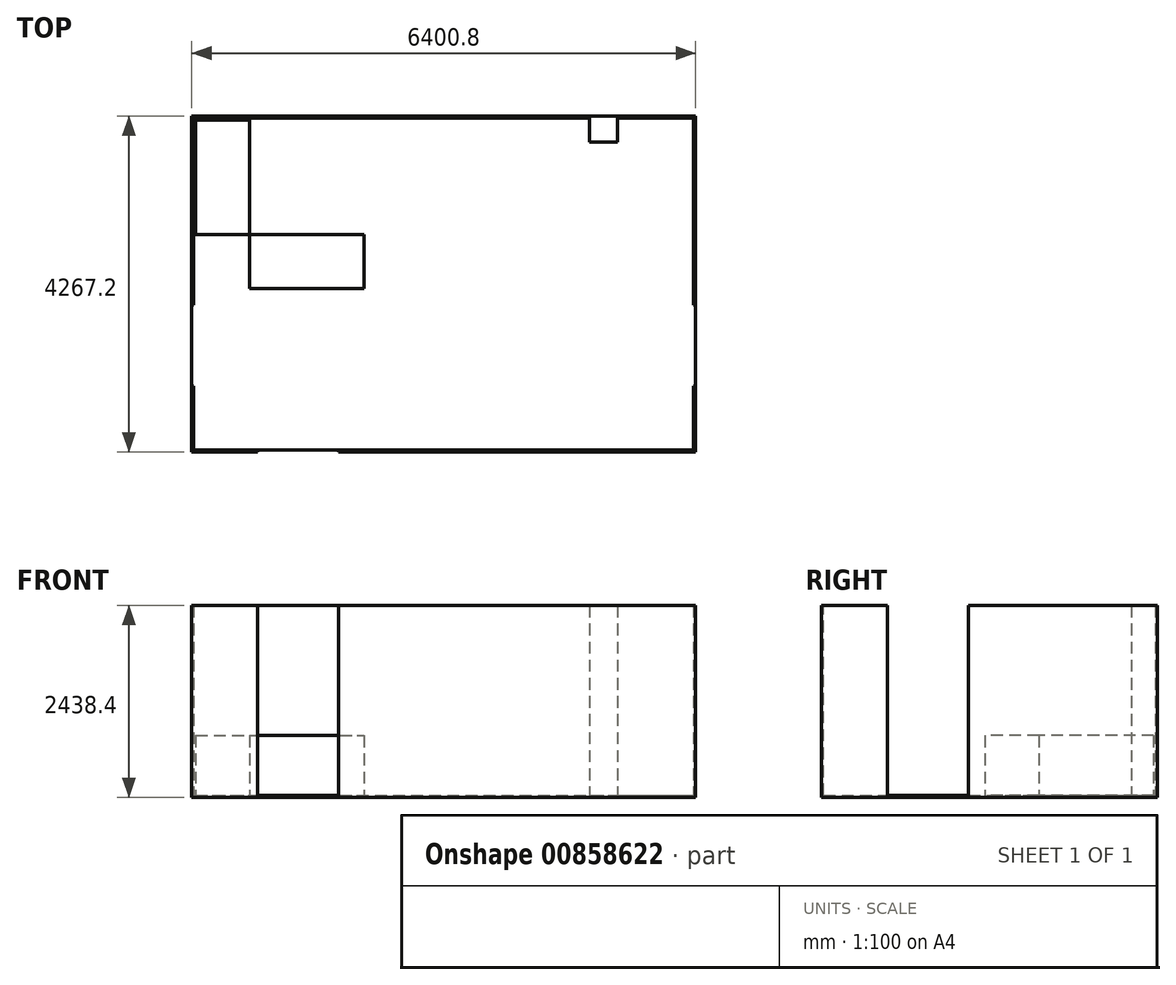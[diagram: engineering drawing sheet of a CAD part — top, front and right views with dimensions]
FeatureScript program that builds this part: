
annotation { "Feature Type Name" : "Feature", "Feature Type Description" : "" }
export const myFeature = defineFeature(function(context is Context, id is Id, definition is map)
    precondition{}
    {
        {
            var Q0;
            Q0=qCreatedBy(makeId("Top.planeOp"),FACE);
            var sketch = newSketch(context, id + "F0", { "sketchPlane" : qUnion([Q0])});
            skLineSegment(sketch, "E0.bottom", {"start": v(-3200.4, -2133.6) * mm, "end": v(3200.4, -2133.6) * mm});
            skLineSegment(sketch, "E0.top", {"start": v(-3200.4, 2133.6) * mm, "end": v(3200.4, 2133.6) * mm});
            skLineSegment(sketch, "E0.left", {"start": v(-3200.4, -2133.6) * mm, "end": v(-3200.4, 2133.6) * mm});
            skLineSegment(sketch, "E0.right", {"start": v(3200.4, -2133.6) * mm, "end": v(3200.4, 2133.6) * mm});
            skSolve(sketch);
        }
        {
            var Q0;
            Q0=makeQuery(id+"F0.imprint","IMPRINT",FACE,{"disambiguationData":[TD([[makeQuery(id+"F0.imprint","IMPRINT",EDGE,{"derivedFrom":sQuery(id+"F0.wireOp",EDGE,"E0.bottom")}),1.0]])]});
            extrude(context, id + "F1", {"entities" : qUnion([Q0]), "depth" : 2438.4 * mm, "offsetDistance" : 25.4 * mm});
        }
        {
            var Q0;
            Q0=makeQuery(id+"F1.opExtrude","CAP_FACE",FACE,{"disambiguationData":[OSD([sQuery(id+"F0.wireOp",EDGE,"E0.bottom"),sQuery(id+"F0.wireOp",EDGE,"E0.top"),sQuery(id+"F0.wireOp",EDGE,"E0.left"),sQuery(id+"F0.wireOp",EDGE,"E0.right")])],"isStart":false});
            shell(context, id + "F2", {"entities" : qUnion([Q0]), "thickness" : 25.4 * mm});
        }
        {
            var Q0;
            Q0=makeQuery(id+"F1.opExtrude","SWEPT_FACE",FACE,{"disambiguationData":[OSD([sQuery(id+"F0.wireOp",EDGE,"E0.right")])]});
            var sketch = newSketch(context, id + "F3", { "sketchPlane" : qUnion([Q0])});
            skLineSegment(sketch, "E1.0", {"start": v(-2133.6, 2438.4) * mm, "end": v(-2133.6, 0) * mm});
            skLineSegment(sketch, "E2.0", {"start": v(-2133.6, 0) * mm, "end": v(2133.6, 0) * mm});
            skLineSegment(sketch, "E3.bottom", {"start": v(-1295.4, 25.4) * mm, "end": v(-266.7, 25.4) * mm});
            skLineSegment(sketch, "E3.top", {"start": v(-1295.4, 2438.4) * mm, "end": v(-266.7, 2438.4) * mm});
            skLineSegment(sketch, "E3.left", {"start": v(-1295.4, 25.4) * mm, "end": v(-1295.4, 2438.4) * mm});
            skLineSegment(sketch, "E3.right", {"start": v(-266.7, 25.4) * mm, "end": v(-266.7, 2438.4) * mm});
            skSolve(sketch);
        }
        {
            var Q0;
            Q0 = qSketchRegion(id + "F3", true);
            var Q1;
            Q1=makeQuery(id+"F1.opExtrude","SWEPT_FACE",FACE,{"disambiguationData":[OSD([sQuery(id+"F0.wireOp",EDGE,"E0.left")])]});
            extrude(context, id + "F4", {"entities" : qUnion([Q0]), "operationType" : NewBodyOperationType.REMOVE, "endBound" : BoundingType.UP_TO_SURFACE, "oppositeDirection" : true, "depth" : 25.4 * mm, "endBoundEntityFace" : qUnion([Q1]), "offsetDistance" : 25.4 * mm});
        }
        {
            var Q0;
            Q0=makeQuery(id+"F1.opExtrude","SWEPT_FACE",FACE,{"disambiguationData":[OSD([sQuery(id+"F0.wireOp",EDGE,"E0.bottom")])]});
            var sketch = newSketch(context, id + "F5", { "sketchPlane" : qUnion([Q0])});
            skLineSegment(sketch, "E4.0", {"start": v(-3200.4, 2438.4) * mm, "end": v(-3200.4, 0) * mm});
            skLineSegment(sketch, "E5.0", {"start": v(-3200.4, 0) * mm, "end": v(3200.4, 0) * mm});
            skLineSegment(sketch, "E6.bottom", {"start": v(-2362.2, 0) * mm, "end": v(-1333.5, 0) * mm});
            skLineSegment(sketch, "E6.top", {"start": v(-2362.2, 2438.4) * mm, "end": v(-1333.5, 2438.4) * mm});
            skLineSegment(sketch, "E6.left", {"start": v(-2362.2, 0) * mm, "end": v(-2362.2, 2438.4) * mm});
            skLineSegment(sketch, "E6.right", {"start": v(-1333.5, 0) * mm, "end": v(-1333.5, 2438.4) * mm});
            skSolve(sketch);
        }
        {
            var Q0;
            Q0 = qSketchRegion(id + "F5", true);
            extrude(context, id + "F6", {"entities" : qUnion([Q0]), "operationType" : NewBodyOperationType.REMOVE, "oppositeDirection" : true, "depth" : 25.4 * mm, "offsetDistance" : 25.4 * mm});
        }
        {
            var Q0;
            Q0=makeQuery(id+"F2.opShell","OFFSET_FACE",FACE,{"disambiguationData":[OSD([sQuery(id+"F0.wireOp",EDGE,"E0.bottom"),sQuery(id+"F0.wireOp",EDGE,"E0.top"),sQuery(id+"F0.wireOp",EDGE,"E0.left"),sQuery(id+"F0.wireOp",EDGE,"E0.right")])]});
            var sketch = newSketch(context, id + "F7", { "sketchPlane" : qUnion([Q0])});
            skLineSegment(sketch, "E7.0", {"start": v(-3175, 2108.2) * mm, "end": v(3175, 2108.2) * mm});
            skLineSegment(sketch, "E8.0", {"start": v(3175, -266.7) * mm, "end": v(3175, 2108.2) * mm});
            skLineSegment(sketch, "E9.0", {"start": v(-3175, -2108.2) * mm, "end": v(-3175, 2108.2) * mm});
            skLineSegment(sketch, "E10.bottom", {"start": v(1854.2, 2108.2) * mm, "end": v(2209.8, 2108.2) * mm});
            skLineSegment(sketch, "E10.top", {"start": v(1854.2, 1803.4) * mm, "end": v(2209.8, 1803.4) * mm});
            skLineSegment(sketch, "E10.left", {"start": v(1854.2, 2108.2) * mm, "end": v(1854.2, 1803.4) * mm});
            skLineSegment(sketch, "E10.right", {"start": v(2209.8, 2108.2) * mm, "end": v(2209.8, 1803.4) * mm});
            skSolve(sketch);
        }
        {
            var Q0;
            Q0 = qSketchRegion(id + "F7", true);
            var Q1;
            {var subQ0=sQuery(id+"F0.wireOp",EDGE,"E0.right");var subQ1=sQuery(id+"F0.wireOp",EDGE,"E0.left");var subQ2=sQuery(id+"F0.wireOp",EDGE,"E0.top");Q1=makeQuery(id+"F4.boolean.opBoolean","SPLIT",FACE,{"disambiguationData":[TD([makeQuery(id+"F1.opExtrude","SWEPT_FACE",FACE,{"disambiguationData":[OSD([subQ2])]})])],"derivedFrom":makeQuery(id+"F1.opExtrude","CAP_FACE",FACE,{"disambiguationData":[OSD([sQuery(id+"F0.wireOp",EDGE,"E0.bottom"),subQ2,subQ1,subQ0])],"isStart":false})});}
            extrude(context, id + "F8", {"entities" : qUnion([Q0]), "operationType" : NewBodyOperationType.ADD, "endBound" : BoundingType.UP_TO_SURFACE, "depth" : 25.4 * mm, "endBoundEntityFace" : qUnion([Q1]), "offsetDistance" : 25.4 * mm});
        }
        {
            var Q0;
            Q0=makeQuery(id+"F2.opShell","OFFSET_FACE",FACE,{"disambiguationData":[OSD([sQuery(id+"F0.wireOp",EDGE,"E0.bottom"),sQuery(id+"F0.wireOp",EDGE,"E0.top"),sQuery(id+"F0.wireOp",EDGE,"E0.left"),sQuery(id+"F0.wireOp",EDGE,"E0.right")])]});
            var sketch = newSketch(context, id + "F9", { "sketchPlane" : qUnion([Q0])});
            skLineSegment(sketch, "E11.0", {"start": v(-3175, 2108.2) * mm, "end": v(1854.2, 2108.2) * mm});
            skLineSegment(sketch, "E12.0", {"start": v(-3175, -2108.2) * mm, "end": v(-3175, 2108.2) * mm});
            skLineSegment(sketch, "E13.bottom", {"start": v(-3149.6, 2082.8) * mm, "end": v(-2463.8, 2082.8) * mm});
            skLineSegment(sketch, "E13.top", {"start": v(-3149.6, 628.65) * mm, "end": v(-2463.8, 628.65) * mm});
            skLineSegment(sketch, "E13.left", {"start": v(-3149.6, 2082.8) * mm, "end": v(-3149.6, 628.65) * mm});
            skLineSegment(sketch, "E13.right", {"start": v(-2463.8, 2082.8) * mm, "end": v(-2463.8, 628.65) * mm});
            skSolve(sketch);
        }
        {
            var Q0;
            Q0 = qSketchRegion(id + "F9", true);
            extrude(context, id + "F10", {"entities" : qUnion([Q0]), "depth" : 762 * mm, "offsetDistance" : 25.4 * mm});
        }
        {
            var Q0;
            Q0=makeQuery(id+"F2.opShell","OFFSET_FACE",FACE,{"disambiguationData":[OSD([sQuery(id+"F0.wireOp",EDGE,"E0.bottom"),sQuery(id+"F0.wireOp",EDGE,"E0.top"),sQuery(id+"F0.wireOp",EDGE,"E0.left"),sQuery(id+"F0.wireOp",EDGE,"E0.right")])]});
            var sketch = newSketch(context, id + "F11", { "sketchPlane" : qUnion([Q0])});
            skLineSegment(sketch, "E14.0", {"start": v(-2463.8, 2082.8) * mm, "end": v(-2463.8, 628.65) * mm});
            skLineSegment(sketch, "E15.0", {"start": v(-3149.6, 628.65) * mm, "end": v(-2463.8, 628.65) * mm});
            skLineSegment(sketch, "E16.bottom", {"start": v(-2463.8, 628.65) * mm, "end": v(-1009.65, 628.65) * mm});
            skLineSegment(sketch, "E16.top", {"start": v(-2463.8, -57.15) * mm, "end": v(-1009.65, -57.15) * mm});
            skLineSegment(sketch, "E16.left", {"start": v(-2463.8, 628.65) * mm, "end": v(-2463.8, -57.15) * mm});
            skLineSegment(sketch, "E16.right", {"start": v(-1009.65, 628.65) * mm, "end": v(-1009.65, -57.15) * mm});
            skSolve(sketch);
        }
        {
            var Q0;
            Q0 = qSketchRegion(id + "F11", true);
            extrude(context, id + "F12", {"entities" : qUnion([Q0]), "depth" : 762 * mm, "offsetDistance" : 25.4 * mm});
        }
    });
